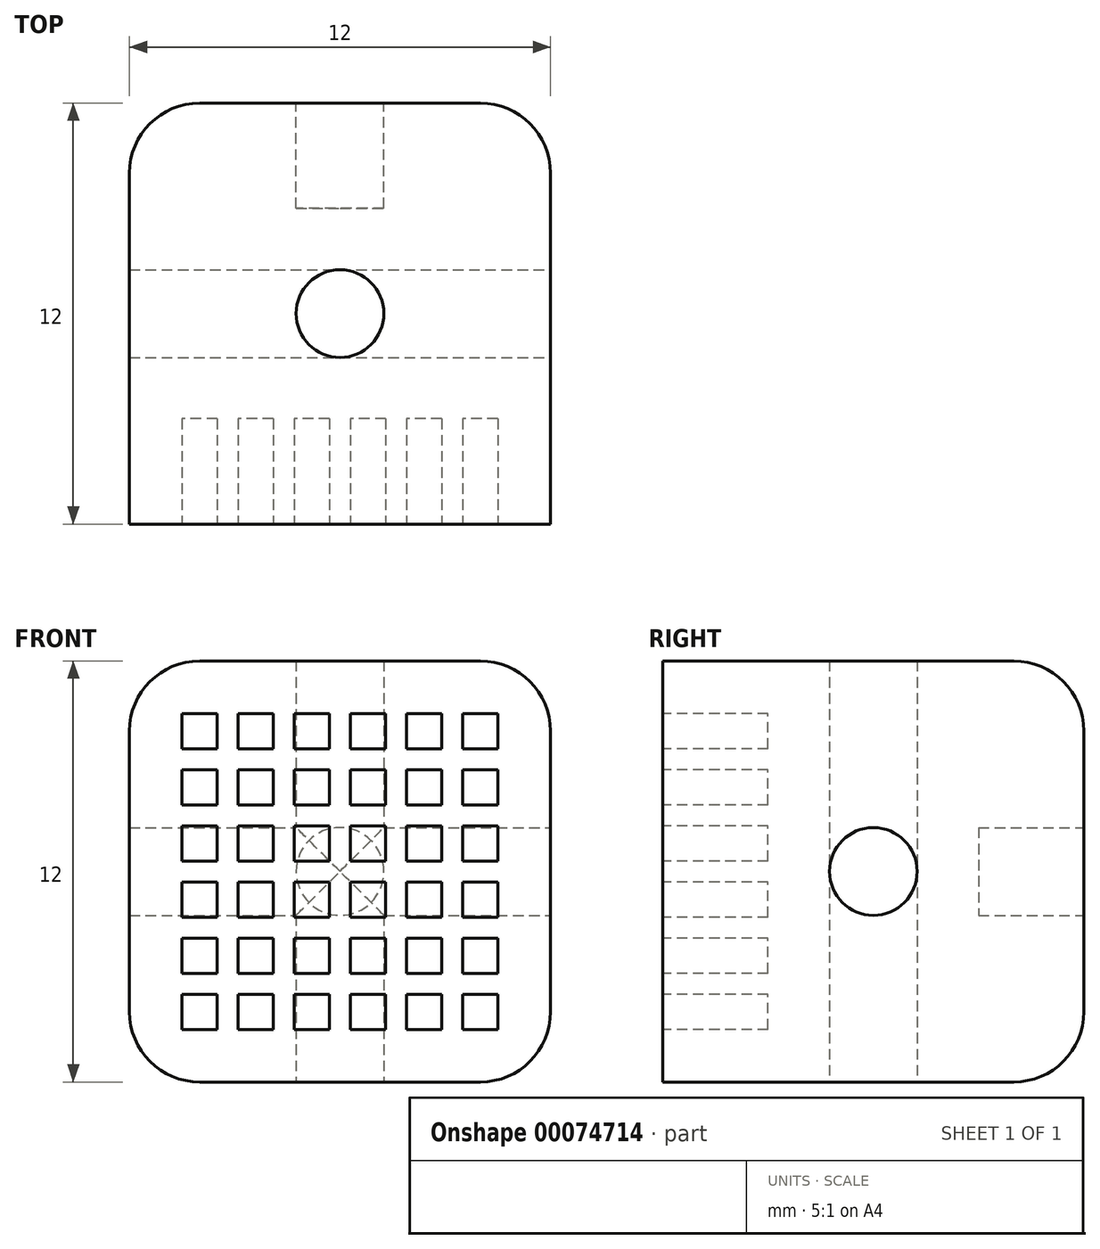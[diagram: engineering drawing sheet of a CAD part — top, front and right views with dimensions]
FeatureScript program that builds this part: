
annotation { "Feature Type Name" : "Feature", "Feature Type Description" : "" }
export const myFeature = defineFeature(function(context is Context, id is Id, definition is map)
    precondition{}
    {
        {
            var Q0;
            Q0=qCreatedBy(makeId("Right.planeOp"),FACE);
            var sketch = newSketch(context, id + "F0", { "sketchPlane" : qUnion([Q0])});
            skLineSegment(sketch, "E0.rect.bottom", {"start": v(6, -6) * mm, "end": v(-6, -6) * mm});
            skLineSegment(sketch, "E0.rect.top", {"start": v(6, 6) * mm, "end": v(-6, 6) * mm});
            skLineSegment(sketch, "E0.rect.left", {"start": v(6, -6) * mm, "end": v(6, 6) * mm});
            skLineSegment(sketch, "E0.rect.right", {"start": v(-6, -6) * mm, "end": v(-6, 6) * mm});
            skPoint(sketch, "E0.rect.middle", {"position": v(0, 0) * mm});
            skSolve(sketch);
        }
        {
            var Q0;
            Q0=qSketchRegion(id+"F0",true);
            extrude(context, id + "F1", {"entities" : qUnion([Q0]), "endBound" : BoundingType.SYMMETRIC, "depth" : 12 * mm});
        }
        {
            var Q0;
            Q0=makeQuery(id+"F1.opExtrude","CAP_FACE",FACE,{"disambiguationData":[OSD([sQuery(id+"F0.wireOp",EDGE,"E0.rect.bottom"),sQuery(id+"F0.wireOp",EDGE,"E0.rect.top"),sQuery(id+"F0.wireOp",EDGE,"E0.rect.left"),sQuery(id+"F0.wireOp",EDGE,"E0.rect.right")])],"isStart":false});
            var sketch = newSketch(context, id + "F2", { "sketchPlane" : qUnion([Q0])});
            skCircle(sketch, "E1", {"center": v(0, 0) * mm, "radius": 1.25 * mm});
            skSolve(sketch);
        }
        {
            var Q0;
            Q0=qSketchRegion(id+"F2",true);
            extrude(context, id + "F3", {"entities" : qUnion([Q0]), "operationType" : NewBodyOperationType.REMOVE, "endBound" : BoundingType.THROUGH_ALL, "oppositeDirection" : true, "depth" : 25 * mm});
        }
        {
            var Q0;
            Q0=makeQuery(id+"F1.opExtrude","SWEPT_FACE",FACE,{"disambiguationData":[OSD([sQuery(id+"F0.wireOp",EDGE,"E0.rect.left")])]});
            var sketch = newSketch(context, id + "F4", { "sketchPlane" : qUnion([Q0])});
            skCircle(sketch, "E2", {"center": v(0, 0) * mm, "radius": 1.25 * mm});
            skSolve(sketch);
        }
        {
            var Q0;
            Q0=qSketchRegion(id+"F4",true);
            extrude(context, id + "F5", {"entities" : qUnion([Q0]), "operationType" : NewBodyOperationType.REMOVE, "oppositeDirection" : true, "depth" : 3 * mm});
        }
        {
            var Q0;
            Q0=makeQuery(id+"F1.opExtrude","SWEPT_FACE",FACE,{"disambiguationData":[OSD([sQuery(id+"F0.wireOp",EDGE,"E0.rect.bottom")])]});
            var sketch = newSketch(context, id + "F6", { "sketchPlane" : qUnion([Q0])});
            skCircle(sketch, "E3", {"center": v(0, 0) * mm, "radius": 1.25 * mm});
            skSolve(sketch);
        }
        {
            var Q0;
            Q0=qSketchRegion(id+"F6",true);
            extrude(context, id + "F7", {"entities" : qUnion([Q0]), "operationType" : NewBodyOperationType.REMOVE, "oppositeDirection" : true, "depth" : 25 * mm});
        }
        {
            var Q0;
            Q0=makeQuery(id+"F1.opExtrude","CAP_EDGE",EDGE,{"disambiguationData":[OSD([sQuery(id+"F0.wireOp",EDGE,"E0.rect.left")])],"isStart":false});
            var Q1;
            Q1=makeQuery(id+"F1.opExtrude","CAP_EDGE",EDGE,{"disambiguationData":[OSD([sQuery(id+"F0.wireOp",EDGE,"E0.rect.left")])],"isStart":true});
            var Q2;
            Q2=makeQuery(id+"F1.opExtrude","CAP_EDGE",EDGE,{"disambiguationData":[OSD([sQuery(id+"F0.wireOp",EDGE,"E0.rect.bottom")])],"isStart":true});
            var Q3;
            Q3=makeQuery(id+"F1.opExtrude","CAP_EDGE",EDGE,{"disambiguationData":[OSD([sQuery(id+"F0.wireOp",EDGE,"E0.rect.bottom")])],"isStart":false});
            var Q4;
            Q4=makeQuery(id+"F1.opExtrude","SWEPT_EDGE",EDGE,{"disambiguationData":[OSD([sQuery(id+"F0.wireOp",EDGE,"E0.rect.bottom"),sQuery(id+"F0.wireOp",EDGE,"E0.rect.left")])]});
            var Q5;
            Q5=makeQuery(id+"F1.opExtrude","CAP_EDGE",EDGE,{"disambiguationData":[OSD([sQuery(id+"F0.wireOp",EDGE,"E0.rect.top")])],"isStart":true});
            var Q6;
            Q6=makeQuery(id+"F1.opExtrude","SWEPT_EDGE",EDGE,{"disambiguationData":[OSD([sQuery(id+"F0.wireOp",EDGE,"E0.rect.top"),sQuery(id+"F0.wireOp",EDGE,"E0.rect.left")])]});
            var Q7;
            Q7=makeQuery(id+"F1.opExtrude","CAP_EDGE",EDGE,{"disambiguationData":[OSD([sQuery(id+"F0.wireOp",EDGE,"E0.rect.top")])],"isStart":false});
            fillet(context, id + "F8", {"entities" : qUnion([Q0, Q1, Q2, Q3, Q4, Q5, Q6, Q7]), "radius" : 2 * mm, "tangentPropagation" : true, "allowEdgeOverflow" : false});
        }
        {
            var Q0;
            Q0=makeQuery(id+"F1.opExtrude","SWEPT_FACE",FACE,{"disambiguationData":[OSD([sQuery(id+"F0.wireOp",EDGE,"E0.rect.right")])]});
            var sketch = newSketch(context, id + "F9", { "sketchPlane" : qUnion([Q0])});
            skLineSegment(sketch, "E4.rect.bottom", {"start": v(4, -4) * mm, "end": v(-4, -4) * mm, "construction": true});
            skLineSegment(sketch, "E4.rect.top", {"start": v(4, 4) * mm, "end": v(-4, 4) * mm, "construction": true});
            skLineSegment(sketch, "E4.rect.left", {"start": v(4, -4) * mm, "end": v(4, 4) * mm, "construction": true});
            skLineSegment(sketch, "E4.rect.right", {"start": v(-4, -4) * mm, "end": v(-4, 4) * mm, "construction": true});
            skPoint(sketch, "E4.rect.middle", {"position": v(0, 0) * mm});
            skLineSegment(sketch, "E5.rect.bottom", {"start": v(-3.5, 3.5) * mm, "end": v(-4.5, 3.5) * mm});
            skLineSegment(sketch, "E5.rect.top", {"start": v(-3.5, 4.5) * mm, "end": v(-4.5, 4.5) * mm});
            skLineSegment(sketch, "E5.rect.left", {"start": v(-3.5, 3.5) * mm, "end": v(-3.5, 4.5) * mm});
            skLineSegment(sketch, "E5.rect.right", {"start": v(-4.5, 3.5) * mm, "end": v(-4.5, 4.5) * mm});
            skPoint(sketch, "E5.rect.middle", {"position": v(-4, 4) * mm});
            skLineSegment(sketch, "E6.0.1.0", {"start": v(-3.5, 1.9) * mm, "end": v(-3.5, 2.9) * mm});
            skLineSegment(sketch, "E6.0.1.1", {"start": v(-3.5, 2.9) * mm, "end": v(-4.5, 2.9) * mm});
            skLineSegment(sketch, "E6.0.1.2", {"start": v(-4.5, 1.9) * mm, "end": v(-4.5, 2.9) * mm});
            skLineSegment(sketch, "E6.0.1.3", {"start": v(-3.5, 1.9) * mm, "end": v(-4.5, 1.9) * mm});
            skLineSegment(sketch, "E6.0.2.0", {"start": v(-3.5, 0.3) * mm, "end": v(-3.5, 1.3) * mm});
            skLineSegment(sketch, "E6.0.2.1", {"start": v(-3.5, 1.3) * mm, "end": v(-4.5, 1.3) * mm});
            skLineSegment(sketch, "E6.0.2.2", {"start": v(-4.5, 0.3) * mm, "end": v(-4.5, 1.3) * mm});
            skLineSegment(sketch, "E6.0.2.3", {"start": v(-3.5, 0.3) * mm, "end": v(-4.5, 0.3) * mm});
            skLineSegment(sketch, "E6.0.3.0", {"start": v(-3.5, -1.3) * mm, "end": v(-3.5, -0.3) * mm});
            skLineSegment(sketch, "E6.0.3.1", {"start": v(-3.5, -0.3) * mm, "end": v(-4.5, -0.3) * mm});
            skLineSegment(sketch, "E6.0.3.2", {"start": v(-4.5, -1.3) * mm, "end": v(-4.5, -0.3) * mm});
            skLineSegment(sketch, "E6.0.3.3", {"start": v(-3.5, -1.3) * mm, "end": v(-4.5, -1.3) * mm});
            skLineSegment(sketch, "E6.0.4.0", {"start": v(-3.5, -2.9) * mm, "end": v(-3.5, -1.9) * mm});
            skLineSegment(sketch, "E6.0.4.1", {"start": v(-3.5, -1.9) * mm, "end": v(-4.5, -1.9) * mm});
            skLineSegment(sketch, "E6.0.4.2", {"start": v(-4.5, -2.9) * mm, "end": v(-4.5, -1.9) * mm});
            skLineSegment(sketch, "E6.0.4.3", {"start": v(-3.5, -2.9) * mm, "end": v(-4.5, -2.9) * mm});
            skLineSegment(sketch, "E6.0.5.0", {"start": v(-3.5, -4.5) * mm, "end": v(-3.5, -3.5) * mm});
            skLineSegment(sketch, "E6.0.5.1", {"start": v(-3.5, -3.5) * mm, "end": v(-4.5, -3.5) * mm});
            skLineSegment(sketch, "E6.0.5.2", {"start": v(-4.5, -4.5) * mm, "end": v(-4.5, -3.5) * mm});
            skLineSegment(sketch, "E6.0.5.3", {"start": v(-3.5, -4.5) * mm, "end": v(-4.5, -4.5) * mm});
            skLineSegment(sketch, "E6.1.0.0", {"start": v(-1.9, 3.5) * mm, "end": v(-1.9, 4.5) * mm});
            skLineSegment(sketch, "E6.1.0.1", {"start": v(-1.9, 4.5) * mm, "end": v(-2.9, 4.5) * mm});
            skLineSegment(sketch, "E6.1.0.2", {"start": v(-2.9, 3.5) * mm, "end": v(-2.9, 4.5) * mm});
            skLineSegment(sketch, "E6.1.0.3", {"start": v(-1.9, 3.5) * mm, "end": v(-2.9, 3.5) * mm});
            skLineSegment(sketch, "E6.1.1.0", {"start": v(-1.9, 1.9) * mm, "end": v(-1.9, 2.9) * mm});
            skLineSegment(sketch, "E6.1.1.1", {"start": v(-1.9, 2.9) * mm, "end": v(-2.9, 2.9) * mm});
            skLineSegment(sketch, "E6.1.1.2", {"start": v(-2.9, 1.9) * mm, "end": v(-2.9, 2.9) * mm});
            skLineSegment(sketch, "E6.1.1.3", {"start": v(-1.9, 1.9) * mm, "end": v(-2.9, 1.9) * mm});
            skLineSegment(sketch, "E6.1.2.0", {"start": v(-1.9, 0.3) * mm, "end": v(-1.9, 1.3) * mm});
            skLineSegment(sketch, "E6.1.2.1", {"start": v(-1.9, 1.3) * mm, "end": v(-2.9, 1.3) * mm});
            skLineSegment(sketch, "E6.1.2.2", {"start": v(-2.9, 0.3) * mm, "end": v(-2.9, 1.3) * mm});
            skLineSegment(sketch, "E6.1.2.3", {"start": v(-1.9, 0.3) * mm, "end": v(-2.9, 0.3) * mm});
            skLineSegment(sketch, "E6.1.3.0", {"start": v(-1.9, -1.3) * mm, "end": v(-1.9, -0.3) * mm});
            skLineSegment(sketch, "E6.1.3.1", {"start": v(-1.9, -0.3) * mm, "end": v(-2.9, -0.3) * mm});
            skLineSegment(sketch, "E6.1.3.2", {"start": v(-2.9, -1.3) * mm, "end": v(-2.9, -0.3) * mm});
            skLineSegment(sketch, "E6.1.3.3", {"start": v(-1.9, -1.3) * mm, "end": v(-2.9, -1.3) * mm});
            skLineSegment(sketch, "E6.1.4.0", {"start": v(-1.9, -2.9) * mm, "end": v(-1.9, -1.9) * mm});
            skLineSegment(sketch, "E6.1.4.1", {"start": v(-1.9, -1.9) * mm, "end": v(-2.9, -1.9) * mm});
            skLineSegment(sketch, "E6.1.4.2", {"start": v(-2.9, -2.9) * mm, "end": v(-2.9, -1.9) * mm});
            skLineSegment(sketch, "E6.1.4.3", {"start": v(-1.9, -2.9) * mm, "end": v(-2.9, -2.9) * mm});
            skLineSegment(sketch, "E6.1.5.0", {"start": v(-1.9, -4.5) * mm, "end": v(-1.9, -3.5) * mm});
            skLineSegment(sketch, "E6.1.5.1", {"start": v(-1.9, -3.5) * mm, "end": v(-2.9, -3.5) * mm});
            skLineSegment(sketch, "E6.1.5.2", {"start": v(-2.9, -4.5) * mm, "end": v(-2.9, -3.5) * mm});
            skLineSegment(sketch, "E6.1.5.3", {"start": v(-1.9, -4.5) * mm, "end": v(-2.9, -4.5) * mm});
            skLineSegment(sketch, "E6.2.0.0", {"start": v(-0.3, 3.5) * mm, "end": v(-0.3, 4.5) * mm});
            skLineSegment(sketch, "E6.2.0.1", {"start": v(-0.3, 4.5) * mm, "end": v(-1.3, 4.5) * mm});
            skLineSegment(sketch, "E6.2.0.2", {"start": v(-1.3, 3.5) * mm, "end": v(-1.3, 4.5) * mm});
            skLineSegment(sketch, "E6.2.0.3", {"start": v(-0.3, 3.5) * mm, "end": v(-1.3, 3.5) * mm});
            skLineSegment(sketch, "E6.2.1.0", {"start": v(-0.3, 1.9) * mm, "end": v(-0.3, 2.9) * mm});
            skLineSegment(sketch, "E6.2.1.1", {"start": v(-0.3, 2.9) * mm, "end": v(-1.3, 2.9) * mm});
            skLineSegment(sketch, "E6.2.1.2", {"start": v(-1.3, 1.9) * mm, "end": v(-1.3, 2.9) * mm});
            skLineSegment(sketch, "E6.2.1.3", {"start": v(-0.3, 1.9) * mm, "end": v(-1.3, 1.9) * mm});
            skLineSegment(sketch, "E6.2.2.0", {"start": v(-0.3, 0.3) * mm, "end": v(-0.3, 1.3) * mm});
            skLineSegment(sketch, "E6.2.2.1", {"start": v(-0.3, 1.3) * mm, "end": v(-1.3, 1.3) * mm});
            skLineSegment(sketch, "E6.2.2.2", {"start": v(-1.3, 0.3) * mm, "end": v(-1.3, 1.3) * mm});
            skLineSegment(sketch, "E6.2.2.3", {"start": v(-0.3, 0.3) * mm, "end": v(-1.3, 0.3) * mm});
            skLineSegment(sketch, "E6.2.3.0", {"start": v(-0.3, -1.3) * mm, "end": v(-0.3, -0.3) * mm});
            skLineSegment(sketch, "E6.2.3.1", {"start": v(-0.3, -0.3) * mm, "end": v(-1.3, -0.3) * mm});
            skLineSegment(sketch, "E6.2.3.2", {"start": v(-1.3, -1.3) * mm, "end": v(-1.3, -0.3) * mm});
            skLineSegment(sketch, "E6.2.3.3", {"start": v(-0.3, -1.3) * mm, "end": v(-1.3, -1.3) * mm});
            skLineSegment(sketch, "E6.2.4.0", {"start": v(-0.3, -2.9) * mm, "end": v(-0.3, -1.9) * mm});
            skLineSegment(sketch, "E6.2.4.1", {"start": v(-0.3, -1.9) * mm, "end": v(-1.3, -1.9) * mm});
            skLineSegment(sketch, "E6.2.4.2", {"start": v(-1.3, -2.9) * mm, "end": v(-1.3, -1.9) * mm});
            skLineSegment(sketch, "E6.2.4.3", {"start": v(-0.3, -2.9) * mm, "end": v(-1.3, -2.9) * mm});
            skLineSegment(sketch, "E6.2.5.0", {"start": v(-0.3, -4.5) * mm, "end": v(-0.3, -3.5) * mm});
            skLineSegment(sketch, "E6.2.5.1", {"start": v(-0.3, -3.5) * mm, "end": v(-1.3, -3.5) * mm});
            skLineSegment(sketch, "E6.2.5.2", {"start": v(-1.3, -4.5) * mm, "end": v(-1.3, -3.5) * mm});
            skLineSegment(sketch, "E6.2.5.3", {"start": v(-0.3, -4.5) * mm, "end": v(-1.3, -4.5) * mm});
            skLineSegment(sketch, "E6.3.0.0", {"start": v(1.3, 3.5) * mm, "end": v(1.3, 4.5) * mm});
            skLineSegment(sketch, "E6.3.0.1", {"start": v(1.3, 4.5) * mm, "end": v(0.3, 4.5) * mm});
            skLineSegment(sketch, "E6.3.0.2", {"start": v(0.3, 3.5) * mm, "end": v(0.3, 4.5) * mm});
            skLineSegment(sketch, "E6.3.0.3", {"start": v(1.3, 3.5) * mm, "end": v(0.3, 3.5) * mm});
            skLineSegment(sketch, "E6.3.1.0", {"start": v(1.3, 1.9) * mm, "end": v(1.3, 2.9) * mm});
            skLineSegment(sketch, "E6.3.1.1", {"start": v(1.3, 2.9) * mm, "end": v(0.3, 2.9) * mm});
            skLineSegment(sketch, "E6.3.1.2", {"start": v(0.3, 1.9) * mm, "end": v(0.3, 2.9) * mm});
            skLineSegment(sketch, "E6.3.1.3", {"start": v(1.3, 1.9) * mm, "end": v(0.3, 1.9) * mm});
            skLineSegment(sketch, "E6.3.2.0", {"start": v(1.3, 0.3) * mm, "end": v(1.3, 1.3) * mm});
            skLineSegment(sketch, "E6.3.2.1", {"start": v(1.3, 1.3) * mm, "end": v(0.3, 1.3) * mm});
            skLineSegment(sketch, "E6.3.2.2", {"start": v(0.3, 0.3) * mm, "end": v(0.3, 1.3) * mm});
            skLineSegment(sketch, "E6.3.2.3", {"start": v(1.3, 0.3) * mm, "end": v(0.3, 0.3) * mm});
            skLineSegment(sketch, "E6.3.3.0", {"start": v(1.3, -1.3) * mm, "end": v(1.3, -0.3) * mm});
            skLineSegment(sketch, "E6.3.3.1", {"start": v(1.3, -0.3) * mm, "end": v(0.3, -0.3) * mm});
            skLineSegment(sketch, "E6.3.3.2", {"start": v(0.3, -1.3) * mm, "end": v(0.3, -0.3) * mm});
            skLineSegment(sketch, "E6.3.3.3", {"start": v(1.3, -1.3) * mm, "end": v(0.3, -1.3) * mm});
            skLineSegment(sketch, "E6.3.4.0", {"start": v(1.3, -2.9) * mm, "end": v(1.3, -1.9) * mm});
            skLineSegment(sketch, "E6.3.4.1", {"start": v(1.3, -1.9) * mm, "end": v(0.3, -1.9) * mm});
            skLineSegment(sketch, "E6.3.4.2", {"start": v(0.3, -2.9) * mm, "end": v(0.3, -1.9) * mm});
            skLineSegment(sketch, "E6.3.4.3", {"start": v(1.3, -2.9) * mm, "end": v(0.3, -2.9) * mm});
            skLineSegment(sketch, "E6.3.5.0", {"start": v(1.3, -4.5) * mm, "end": v(1.3, -3.5) * mm});
            skLineSegment(sketch, "E6.3.5.1", {"start": v(1.3, -3.5) * mm, "end": v(0.3, -3.5) * mm});
            skLineSegment(sketch, "E6.3.5.2", {"start": v(0.3, -4.5) * mm, "end": v(0.3, -3.5) * mm});
            skLineSegment(sketch, "E6.3.5.3", {"start": v(1.3, -4.5) * mm, "end": v(0.3, -4.5) * mm});
            skLineSegment(sketch, "E6.4.0.0", {"start": v(2.9, 3.5) * mm, "end": v(2.9, 4.5) * mm});
            skLineSegment(sketch, "E6.4.0.1", {"start": v(2.9, 4.5) * mm, "end": v(1.9, 4.5) * mm});
            skLineSegment(sketch, "E6.4.0.2", {"start": v(1.9, 3.5) * mm, "end": v(1.9, 4.5) * mm});
            skLineSegment(sketch, "E6.4.0.3", {"start": v(2.9, 3.5) * mm, "end": v(1.9, 3.5) * mm});
            skLineSegment(sketch, "E6.4.1.0", {"start": v(2.9, 1.9) * mm, "end": v(2.9, 2.9) * mm});
            skLineSegment(sketch, "E6.4.1.1", {"start": v(2.9, 2.9) * mm, "end": v(1.9, 2.9) * mm});
            skLineSegment(sketch, "E6.4.1.2", {"start": v(1.9, 1.9) * mm, "end": v(1.9, 2.9) * mm});
            skLineSegment(sketch, "E6.4.1.3", {"start": v(2.9, 1.9) * mm, "end": v(1.9, 1.9) * mm});
            skLineSegment(sketch, "E6.4.2.0", {"start": v(2.9, 0.3) * mm, "end": v(2.9, 1.3) * mm});
            skLineSegment(sketch, "E6.4.2.1", {"start": v(2.9, 1.3) * mm, "end": v(1.9, 1.3) * mm});
            skLineSegment(sketch, "E6.4.2.2", {"start": v(1.9, 0.3) * mm, "end": v(1.9, 1.3) * mm});
            skLineSegment(sketch, "E6.4.2.3", {"start": v(2.9, 0.3) * mm, "end": v(1.9, 0.3) * mm});
            skLineSegment(sketch, "E6.4.3.0", {"start": v(2.9, -1.3) * mm, "end": v(2.9, -0.3) * mm});
            skLineSegment(sketch, "E6.4.3.1", {"start": v(2.9, -0.3) * mm, "end": v(1.9, -0.3) * mm});
            skLineSegment(sketch, "E6.4.3.2", {"start": v(1.9, -1.3) * mm, "end": v(1.9, -0.3) * mm});
            skLineSegment(sketch, "E6.4.3.3", {"start": v(2.9, -1.3) * mm, "end": v(1.9, -1.3) * mm});
            skLineSegment(sketch, "E6.4.4.0", {"start": v(2.9, -2.9) * mm, "end": v(2.9, -1.9) * mm});
            skLineSegment(sketch, "E6.4.4.1", {"start": v(2.9, -1.9) * mm, "end": v(1.9, -1.9) * mm});
            skLineSegment(sketch, "E6.4.4.2", {"start": v(1.9, -2.9) * mm, "end": v(1.9, -1.9) * mm});
            skLineSegment(sketch, "E6.4.4.3", {"start": v(2.9, -2.9) * mm, "end": v(1.9, -2.9) * mm});
            skLineSegment(sketch, "E6.4.5.0", {"start": v(2.9, -4.5) * mm, "end": v(2.9, -3.5) * mm});
            skLineSegment(sketch, "E6.4.5.1", {"start": v(2.9, -3.5) * mm, "end": v(1.9, -3.5) * mm});
            skLineSegment(sketch, "E6.4.5.2", {"start": v(1.9, -4.5) * mm, "end": v(1.9, -3.5) * mm});
            skLineSegment(sketch, "E6.4.5.3", {"start": v(2.9, -4.5) * mm, "end": v(1.9, -4.5) * mm});
            skLineSegment(sketch, "E6.5.0.0", {"start": v(4.5, 3.5) * mm, "end": v(4.5, 4.5) * mm});
            skLineSegment(sketch, "E6.5.0.1", {"start": v(4.5, 4.5) * mm, "end": v(3.5, 4.5) * mm});
            skLineSegment(sketch, "E6.5.0.2", {"start": v(3.5, 3.5) * mm, "end": v(3.5, 4.5) * mm});
            skLineSegment(sketch, "E6.5.0.3", {"start": v(4.5, 3.5) * mm, "end": v(3.5, 3.5) * mm});
            skLineSegment(sketch, "E6.5.1.0", {"start": v(4.5, 1.9) * mm, "end": v(4.5, 2.9) * mm});
            skLineSegment(sketch, "E6.5.1.1", {"start": v(4.5, 2.9) * mm, "end": v(3.5, 2.9) * mm});
            skLineSegment(sketch, "E6.5.1.2", {"start": v(3.5, 1.9) * mm, "end": v(3.5, 2.9) * mm});
            skLineSegment(sketch, "E6.5.1.3", {"start": v(4.5, 1.9) * mm, "end": v(3.5, 1.9) * mm});
            skLineSegment(sketch, "E6.5.2.0", {"start": v(4.5, 0.3) * mm, "end": v(4.5, 1.3) * mm});
            skLineSegment(sketch, "E6.5.2.1", {"start": v(4.5, 1.3) * mm, "end": v(3.5, 1.3) * mm});
            skLineSegment(sketch, "E6.5.2.2", {"start": v(3.5, 0.3) * mm, "end": v(3.5, 1.3) * mm});
            skLineSegment(sketch, "E6.5.2.3", {"start": v(4.5, 0.3) * mm, "end": v(3.5, 0.3) * mm});
            skLineSegment(sketch, "E6.5.3.0", {"start": v(4.5, -1.3) * mm, "end": v(4.5, -0.3) * mm});
            skLineSegment(sketch, "E6.5.3.1", {"start": v(4.5, -0.3) * mm, "end": v(3.5, -0.3) * mm});
            skLineSegment(sketch, "E6.5.3.2", {"start": v(3.5, -1.3) * mm, "end": v(3.5, -0.3) * mm});
            skLineSegment(sketch, "E6.5.3.3", {"start": v(4.5, -1.3) * mm, "end": v(3.5, -1.3) * mm});
            skLineSegment(sketch, "E6.5.4.0", {"start": v(4.5, -2.9) * mm, "end": v(4.5, -1.9) * mm});
            skLineSegment(sketch, "E6.5.4.1", {"start": v(4.5, -1.9) * mm, "end": v(3.5, -1.9) * mm});
            skLineSegment(sketch, "E6.5.4.2", {"start": v(3.5, -2.9) * mm, "end": v(3.5, -1.9) * mm});
            skLineSegment(sketch, "E6.5.4.3", {"start": v(4.5, -2.9) * mm, "end": v(3.5, -2.9) * mm});
            skLineSegment(sketch, "E6.5.5.0", {"start": v(4.5, -4.5) * mm, "end": v(4.5, -3.5) * mm});
            skLineSegment(sketch, "E6.5.5.1", {"start": v(4.5, -3.5) * mm, "end": v(3.5, -3.5) * mm});
            skLineSegment(sketch, "E6.5.5.2", {"start": v(3.5, -4.5) * mm, "end": v(3.5, -3.5) * mm});
            skLineSegment(sketch, "E6.5.5.3", {"start": v(4.5, -4.5) * mm, "end": v(3.5, -4.5) * mm});
            skLineSegment(sketch, "E6.direction1", {"start": v(-3.5, 3.5) * mm, "end": v(-1.9, 3.5) * mm, "construction": true});
            skLineSegment(sketch, "E6.direction2", {"start": v(-3.5, 3.5) * mm, "end": v(-3.5, 1.9) * mm, "construction": true});
            skLineSegment(sketch, "E7", {"start": v(3.5, 4.5) * mm, "end": v(4.5, 3.5) * mm, "construction": true});
            skSolve(sketch);
        }
        {
            var Q0;
            Q0=qSketchRegion(id+"F9",true);
            extrude(context, id + "F10", {"entities" : qUnion([Q0]), "operationType" : NewBodyOperationType.REMOVE, "oppositeDirection" : true, "depth" : 3 * mm});
        }
    });
